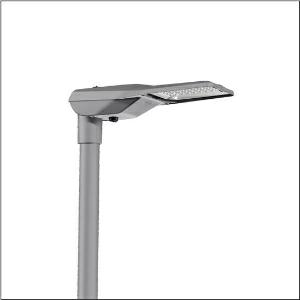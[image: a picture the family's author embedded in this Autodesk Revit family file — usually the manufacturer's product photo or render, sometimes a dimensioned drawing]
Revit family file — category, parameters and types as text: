
# Revit family: streetlight_sl_21_mini___p1_0a_5xe2a33t08gb_80ca
name_source: partatom
category: Lighting Fixtures
units: mm (PartAtom-declared; Revit-internal decimal feet)

## family parameters
Cut with Voids When Loaded = No
Host = Face
Light Source = No
Part Type = Normal
Room Calculation Point = No
Round Connector Dimension = Use Diameter
Shared = No

## types (1)
- --- (1 x LED, 5940 lm, 40.4 W, 3000K)
    Apparent Load = 40 VA
    CIE Flux Codes = 21 50 90 100 100
    Color Rendering = 70
    Color Temperature = 3000K
    Default Elevation = 1800 mm
    Description = Streetlight SL 21 mini, mast luminaire, primary light control with lens, of PMMA, primary optical cover: cover, of toughened safety glass, transparent, light distribution: P1.0a, light emission: direct distribution, primary light characteristic: asymmetric, installation type: side-entry, post-top, LED, High Power LED, rated luminous flux: 5.940lm, luminous efficacy: 147lm/W, light colour: 730, colour temperature: 3000K, control gear: D4i, control: overheat protection, constant luminous flux control, time-dependent luminous flux control, flexible luminous flux parameterisation, pre-setting: logarithmic dimming characteristic, mains connection: 220..240V, AC, 50/60Hz, start of lifetime: 40W, end of service life: 41W, reduction: 19W, luminaire housing, of diecast aluminium, powder-coated, SITECO metallic grey (DB 702S), corrosivity category C5 high according to DIN EN ISO 12944, please order mast flange separately, inclination adjustable: 0°, 5°, 10°, 15°, sealing non-destructively replaceable, multi-level sealing system, length: 628mm, width: 235mm, height: 110mm, mast flange for spigot size: 42mm (side-entry): 5XC10008XM4, 60/48mm (side-entry/post-top): 5XC10108XM2, 76/60mm (side-entry/post-top): 5XC10108XM1, mounting height: 4..8m, Smart Interface below and above, protection rating (complete): IP66, insulation class (complete): insulation class II (safety insulation), certification: CE, ENEC, ENEC+, VDE, impact resistance: IK10, permissible operating ambient temperature for outdoor applications: -40..+50°C, standard-compliant lighting for roads and squares, packaging unit: 1 piece

Light Distribution: P1.0a
    Height = 110 mm
    Lamp = 1 x LED
    Lamp Light Flux = 5940 lm
    Lamp Power = 40.4 W
    Lamp count = 1
    Length = 625 mm
    Luminous efficacy = 147 lm/W
    Manufacturer = Siteco
    ModVariant = No
    Model = 5XE2A33T08GB
    Mounting Place = Pole
    Mounting Type = Pole top
    Number of Poles = 1
    OnlyDefault = Yes
    Power Factor = 1
    Product Name = Streetlight SL 21 mini | P1.0a
    Product group = mast luminaire | pylon top
    ProductGroupID = 6100
    Protection Class = Protection class II
    Protection Degree = IP 66
    RLX_Detail_Level = 1
    RLX_Emergency_Light_Flux = 0 lm
    RLX_Emergency_Type = 0
    RLX_Emergency_Type_DB = No
    RlxData = <blob elided: 37577 chars, md5=c405c98c>
    Socket = socket
    Standby Power = 0 W
    System Light Flux = 5940 lm
    System Power = 40 W
    Type Comments = factory setting: luminous flux: 100 % | dim-lin: 254 | 812 mA
    Type Image = l_1003514.jpg
    URL = http://relux.com
    VarID = @adj_185573
    Voltage = 0 V
    Weight = 0.00 kg
    Width = 234 mm

## geometry (parser evidence)
native form markers: Blend x4, Sweep x11
no freeform markers — native parametric forms only
